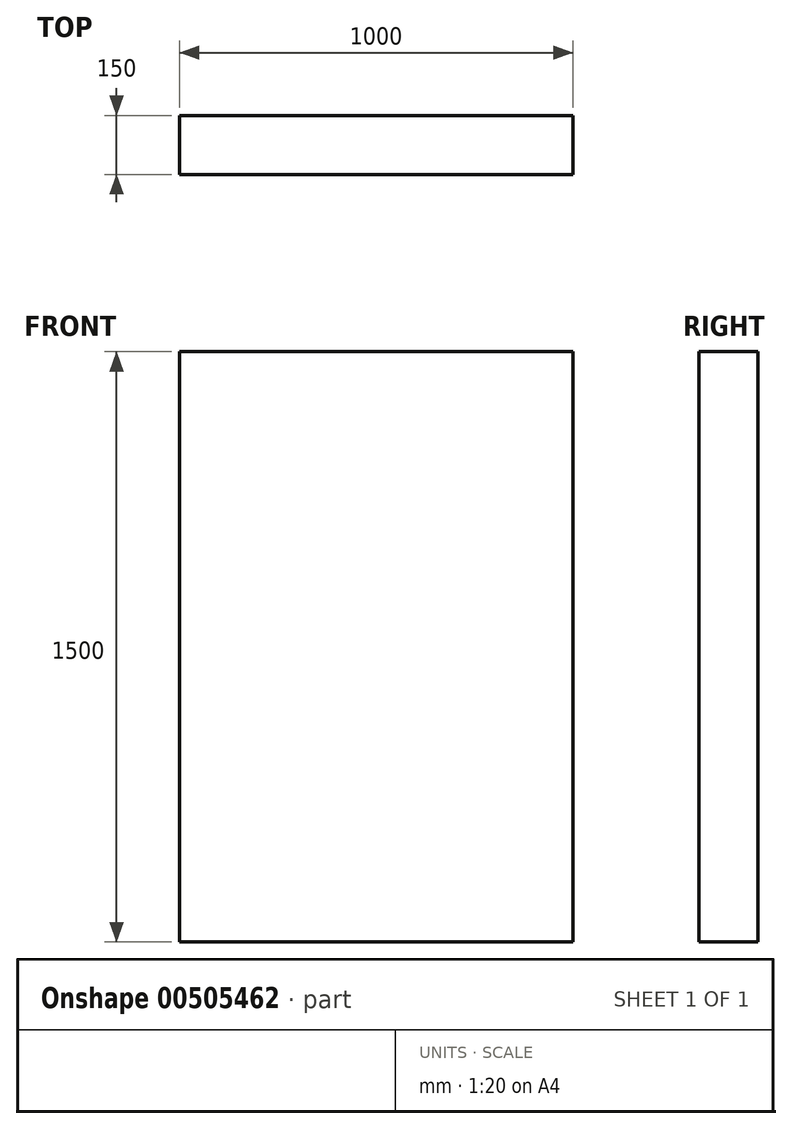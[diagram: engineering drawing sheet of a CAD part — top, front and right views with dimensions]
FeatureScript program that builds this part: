
annotation { "Feature Type Name" : "Feature", "Feature Type Description" : "" }
export const myFeature = defineFeature(function(context is Context, id is Id, definition is map)
    precondition{}
    {
        {
            var Q0;
            Q0=qCreatedBy(makeId("Top.planeOp"),FACE);
            var sketch = newSketch(context, id + "F0", { "sketchPlane" : qUnion([Q0])});
            skLineSegment(sketch, "E0.bottom", {"start": v(0, 0) * mm, "end": v(-1000, 0) * mm});
            skLineSegment(sketch, "E0.top", {"start": v(0, -150) * mm, "end": v(-1000, -150) * mm});
            skLineSegment(sketch, "E0.left", {"start": v(0, 0) * mm, "end": v(0, -150) * mm});
            skLineSegment(sketch, "E0.right", {"start": v(-1000, 0) * mm, "end": v(-1000, -150) * mm});
            skSolve(sketch);
        }
        {
            var Q0;
            Q0 = qSketchRegion(id + "F0", true);
            extrude(context, id + "F1", {"entities" : qUnion([Q0]), "depth" : 1500 * mm});
        }
    });
